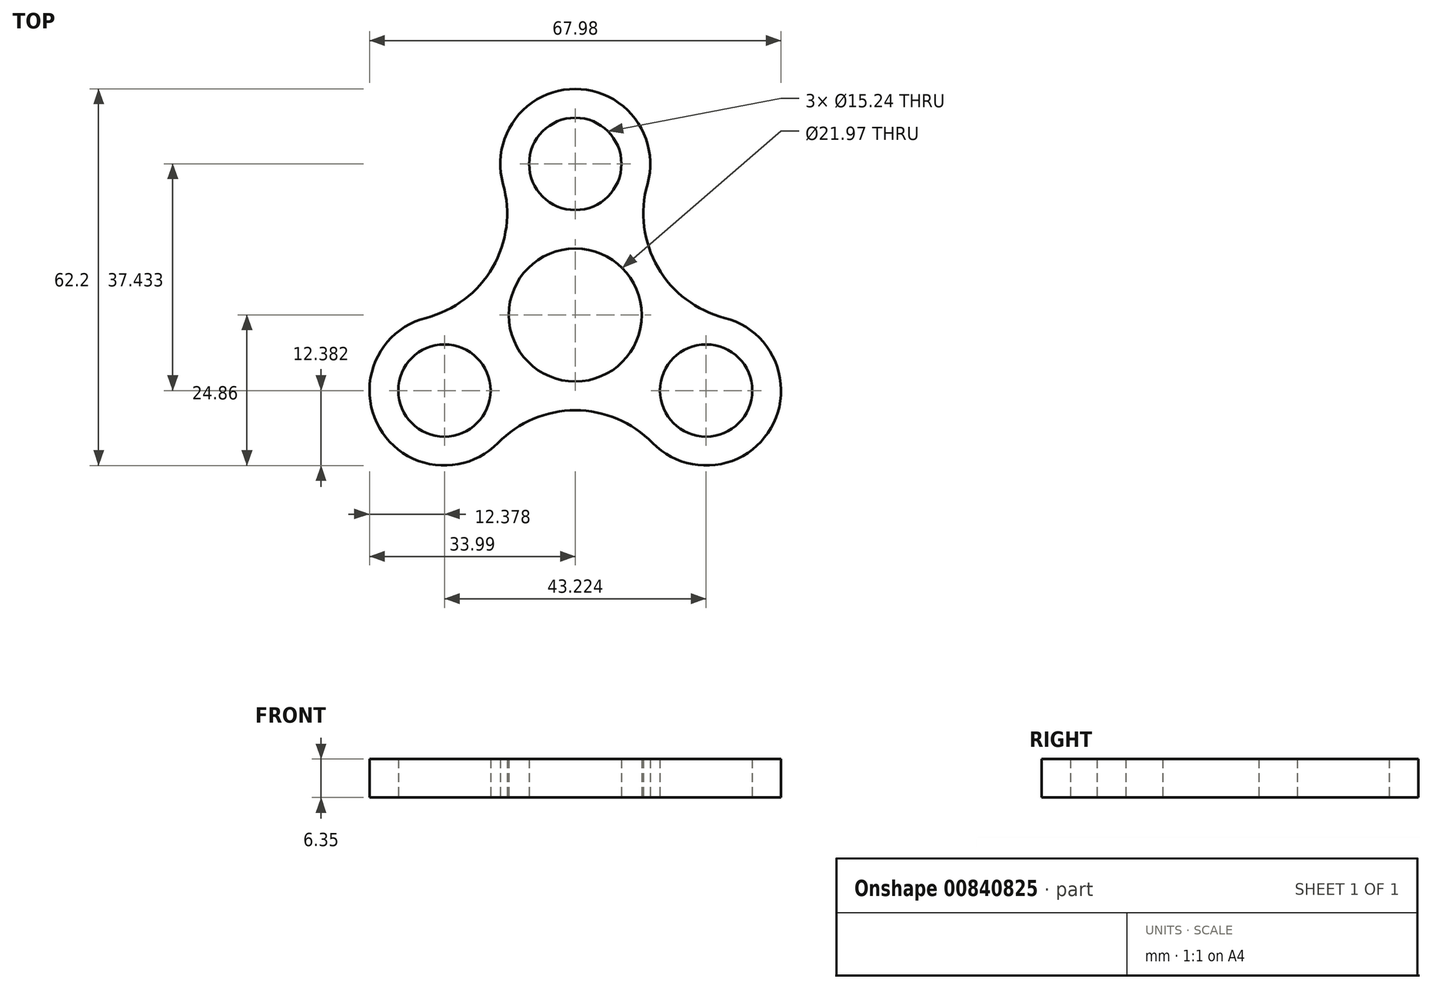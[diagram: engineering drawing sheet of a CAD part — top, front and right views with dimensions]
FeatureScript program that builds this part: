
annotation { "Feature Type Name" : "Feature", "Feature Type Description" : "" }
export const myFeature = defineFeature(function(context is Context, id is Id, definition is map)
    precondition{}
    {
        {
            var Q0;
            Q0=qCreatedBy(makeId("Top.planeOp"),FACE);
            var sketch = newSketch(context, id + "F0", { "sketchPlane" : qUnion([Q0])});
            skCircle(sketch, "E0", {"center": v(0, 0) * mm, "radius": 15.75 * mm, "construction": true});
            skArc(sketch, "E1", {"start": v(12.75, -21.12) * mm, "mid": v(32.34, -18.67) * mm, "end": v(24.67, -0.48) * mm});
            skArc(sketch, "E2", {"start": v(-24.67, -0.48) * mm, "mid": v(-32.34, -18.67) * mm, "end": v(-12.75, -21.12) * mm});
            skArc(sketch, "E3", {"start": v(11.92, 21.6) * mm, "mid": v(0, 37.34) * mm, "end": v(-11.92, 21.6) * mm});
            skLineSegment(sketch, "E4", {"start": v(0, 24.96) * mm, "end": v(0, 0) * mm, "construction": true});
            skLineSegment(sketch, "E5", {"start": v(-21.61, -12.48) * mm, "end": v(0, 0) * mm, "construction": true});
            skLineSegment(sketch, "E6", {"start": v(21.61, -12.48) * mm, "end": v(0, 0) * mm, "construction": true});
            skArc(sketch, "E7", {"start": v(-24.67, -0.48) * mm, "mid": v(-13.64, 7.87) * mm, "end": v(-11.92, 21.6) * mm});
            skArc(sketch, "E8", {"start": v(11.92, 21.6) * mm, "mid": v(13.64, 7.87) * mm, "end": v(24.67, -0.48) * mm});
            skArc(sketch, "E9", {"start": v(12.75, -21.12) * mm, "mid": v(0, -15.75) * mm, "end": v(-12.75, -21.12) * mm});
            skCircle(sketch, "E10", {"center": v(21.61, -12.48) * mm, "radius": 7.62 * mm});
            skCircle(sketch, "E11", {"center": v(-21.61, -12.48) * mm, "radius": 7.62 * mm});
            skCircle(sketch, "E12", {"center": v(0, 24.96) * mm, "radius": 7.62 * mm});
            skCircle(sketch, "E13", {"center": v(0, 0) * mm, "radius": 10.99 * mm});
            skSolve(sketch);
        }
        {
            var Q0;
            Q0 = qSketchRegion(id + "F0", true);
            extrude(context, id + "F1", {"entities" : qUnion([Q0]), "depth" : 6.35 * mm, "offsetDistance" : 25.4 * mm});
        }
    });
